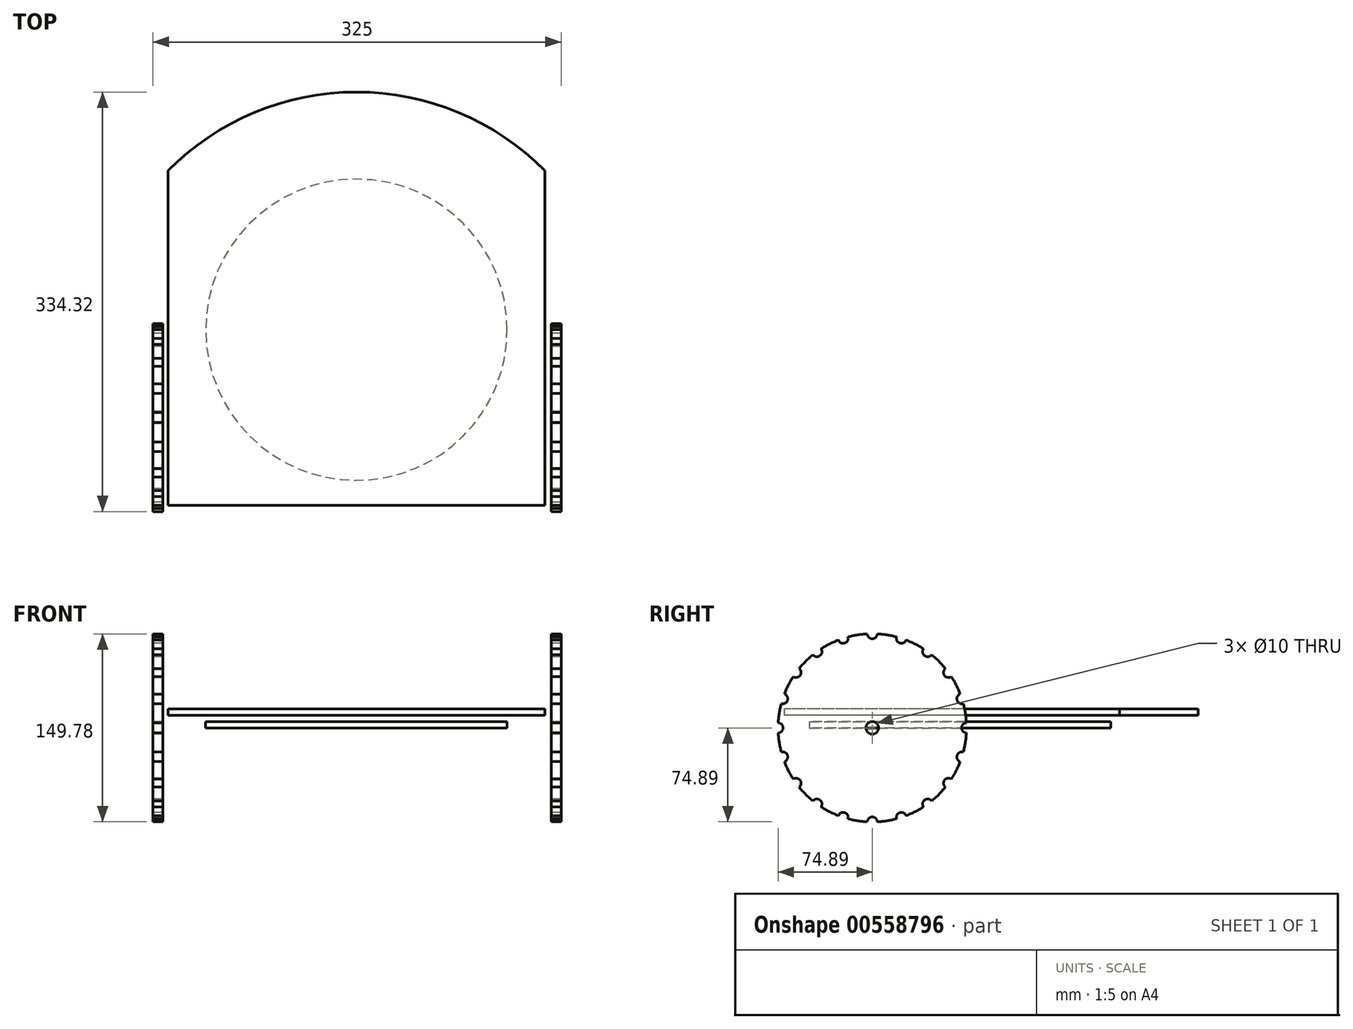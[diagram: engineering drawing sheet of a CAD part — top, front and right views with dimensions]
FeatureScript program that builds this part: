
annotation { "Feature Type Name" : "Feature", "Feature Type Description" : "" }
export const myFeature = defineFeature(function(context is Context, id is Id, definition is map)
    precondition{}
    {
        {
            var Q0;
            Q0=qCreatedBy(makeId("Top.planeOp"),FACE);
            var sketch = newSketch(context, id + "F0", { "sketchPlane" : qUnion([Q0])});
            skCircle(sketch, "E0", {"center": v(0, 0) * mm, "radius": 120 * mm});
            skLineSegment(sketch, "E1.filletArc", {"start": v(150, -145) * mm, "end": v(150, -145) * mm});
            skLineSegment(sketch, "E2", {"start": v(-150, 126.83) * mm, "end": v(150, 126.83) * mm});
            skArc(sketch, "E3", {"start": v(150, 126.83) * mm, "mid": v(0, 189.43) * mm, "end": v(-150, 126.83) * mm});
            skLineSegment(sketch, "E4.top", {"start": v(-150, -140) * mm, "end": v(150, -140) * mm});
            skLineSegment(sketch, "E4.left", {"start": v(-150, 126.83) * mm, "end": v(-150, -140) * mm});
            skLineSegment(sketch, "E4.right", {"start": v(150, 126.83) * mm, "end": v(150, -140) * mm});
            skSolve(sketch);
        }
        {
            var Q0;
            Q0=makeQuery(id+"F0.imprint","IMPRINT",FACE,{"disambiguationData":[TD([[makeQuery(id+"F0.imprint","IMPRINT",EDGE,{"derivedFrom":sQuery(id+"F0.wireOp",EDGE,"E0")}),1.0]])]});
            extrude(context, id + "F1", {"entities" : qUnion([Q0]), "depth" : 5 * mm, "offsetDistance" : 25 * mm});
        }
        {
            var Q0;
            Q0=makeQuery(id+"F0.imprint","IMPRINT",FACE,{"disambiguationData":[TD([[makeQuery(id+"F0.imprint","IMPRINT",EDGE,{"derivedFrom":sQuery(id+"F0.wireOp",EDGE,"E3")}),1.0]])]});
            var Q1;
            Q1=makeQuery(id+"F0.imprint","IMPRINT",FACE,{"disambiguationData":[TD([[makeQuery(id+"F0.imprint","IMPRINT",EDGE,{"derivedFrom":sQuery(id+"F0.wireOp",EDGE,"E0")}),-1.0]])]});
            var Q2;
            Q2=makeQuery(id+"F0.imprint","IMPRINT",FACE,{"disambiguationData":[TD([[makeQuery(id+"F0.imprint","IMPRINT",EDGE,{"derivedFrom":sQuery(id+"F0.wireOp",EDGE,"E0")}),1.0]])]});
            extrude(context, id + "F2", {"entities" : qUnion([Q0, Q1, Q2]), "depth" : 5 * mm, "offsetDistance" : 25 * mm});
        }
        {
            var Q0;
            Q0=makeQuery(id+"F2.opExtrude","SWEPT_BODY",BODY,{"disambiguationData":[OSD([sQuery(id+"F0.wireOp",EDGE,"E3"),sQuery(id+"F0.wireOp",EDGE,"E4.top"),sQuery(id+"F0.wireOp",EDGE,"E4.left"),sQuery(id+"F0.wireOp",EDGE,"E4.right")])]});
            transform(context, id + "F3", {"entities" : qUnion([Q0]), "transformType" : TransformType.TRANSLATION_3D, "dx" : 0 * mm, "dy" : 0 * mm, "dz" : 10 * mm, "makeCopy" : false});
        }
        {
            var Q0;
            Q0=qCreatedBy(makeId("Right.planeOp"),FACE);
            var sketch = newSketch(context, id + "F4", { "sketchPlane" : qUnion([Q0])});
            skCircle(sketch, "E5", {"center": v(0, 0) * mm, "radius": 75 * mm});
            skCircle(sketch, "E6", {"center": v(0, 75) * mm, "radius": 4 * mm});
            skCircle(sketch, "E7.1.0", {"center": v(-23.18, 71.33) * mm, "radius": 4 * mm});
            skCircle(sketch, "E7.2.0", {"center": v(-44.08, 60.68) * mm, "radius": 4 * mm});
            skCircle(sketch, "E7.3.0", {"center": v(-60.68, 44.08) * mm, "radius": 4 * mm});
            skCircle(sketch, "E7.4.0", {"center": v(-71.33, 23.18) * mm, "radius": 4 * mm});
            skCircle(sketch, "E7.5.0", {"center": v(-75, 0) * mm, "radius": 4 * mm});
            skCircle(sketch, "E7.6.0", {"center": v(-71.33, -23.18) * mm, "radius": 4 * mm});
            skCircle(sketch, "E7.7.0", {"center": v(-60.68, -44.08) * mm, "radius": 4 * mm});
            skCircle(sketch, "E7.8.0", {"center": v(-44.08, -60.68) * mm, "radius": 4 * mm});
            skCircle(sketch, "E7.9.0", {"center": v(-23.18, -71.33) * mm, "radius": 4 * mm});
            skCircle(sketch, "E7.10.0", {"center": v(0, -75) * mm, "radius": 4 * mm});
            skCircle(sketch, "E7.11.0", {"center": v(23.18, -71.33) * mm, "radius": 4 * mm});
            skCircle(sketch, "E7.12.0", {"center": v(44.08, -60.68) * mm, "radius": 4 * mm});
            skCircle(sketch, "E7.13.0", {"center": v(60.68, -44.08) * mm, "radius": 4 * mm});
            skCircle(sketch, "E7.14.0", {"center": v(71.33, -23.18) * mm, "radius": 4 * mm});
            skCircle(sketch, "E7.15.0", {"center": v(75, 0) * mm, "radius": 4 * mm});
            skCircle(sketch, "E7.16.0", {"center": v(71.33, 23.18) * mm, "radius": 4 * mm});
            skCircle(sketch, "E7.17.0", {"center": v(60.68, 44.08) * mm, "radius": 4 * mm});
            skCircle(sketch, "E7.18.0", {"center": v(44.08, 60.68) * mm, "radius": 4 * mm});
            skCircle(sketch, "E7.19.0", {"center": v(23.18, 71.33) * mm, "radius": 4 * mm});
            skCircle(sketch, "E8", {"center": v(0, 0) * mm, "radius": 5 * mm});
            skSolve(sketch);
        }
        {
            var Q0;
            {var subQ0=sQuery(id+"F4.wireOp",EDGE,"E5");var subQ40=sQuery(id+"F4.wireOp",EDGE,"E6");var subQ41=makeQuery(id+"F4.imprint","INTERSECT",VERTEX,{"disambiguationData":[OD(0.0)],"derivedFrom":[subQ40,subQ0]});Q0=makeQuery(id+"F4.imprint","IMPRINT",FACE,{"disambiguationData":[TD([[makeQuery(id+"F4.imprint","IMPRINT",EDGE,{"disambiguationData":[TD([[subQ41,1.0]])],"derivedFrom":subQ40}),-1.0]])]});}
            extrude(context, id + "F5", {"entities" : qUnion([Q0]), "depth" : 8 * mm, "offsetDistance" : 25 * mm});
        }
        {
            var Q0;
            Q0=makeQuery(id+"F5.opExtrude","SWEPT_BODY",BODY,{"disambiguationData":[OSD([sQuery(id+"F4.wireOp",EDGE,"E6"),sQuery(id+"F4.wireOp",EDGE,"E7.1.0"),sQuery(id+"F4.wireOp",EDGE,"E7.2.0"),sQuery(id+"F4.wireOp",EDGE,"E7.3.0"),sQuery(id+"F4.wireOp",EDGE,"E7.4.0"),sQuery(id+"F4.wireOp",EDGE,"E7.5.0"),sQuery(id+"F4.wireOp",EDGE,"E7.6.0"),sQuery(id+"F4.wireOp",EDGE,"E7.7.0"),sQuery(id+"F4.wireOp",EDGE,"E7.8.0"),sQuery(id+"F4.wireOp",EDGE,"E7.9.0"),sQuery(id+"F4.wireOp",EDGE,"E7.10.0"),sQuery(id+"F4.wireOp",EDGE,"E7.11.0"),sQuery(id+"F4.wireOp",EDGE,"E7.12.0"),sQuery(id+"F4.wireOp",EDGE,"E7.13.0"),sQuery(id+"F4.wireOp",EDGE,"E7.14.0"),sQuery(id+"F4.wireOp",EDGE,"E7.15.0"),sQuery(id+"F4.wireOp",EDGE,"E7.16.0"),sQuery(id+"F4.wireOp",EDGE,"E7.17.0"),sQuery(id+"F4.wireOp",EDGE,"E7.18.0"),sQuery(id+"F4.wireOp",EDGE,"E7.19.0"),sQuery(id+"F4.wireOp",EDGE,"E5")])]});
            transform(context, id + "F6", {"entities" : qUnion([Q0]), "transformType" : TransformType.TRANSLATION_3D, "dx" : 155 * mm, "dy" : 0 * mm, "dz" : 0 * mm, "makeCopy" : false});
        }
        {
            var Q0;
            Q0=makeQuery(id+"F5.opExtrude","SWEPT_BODY",BODY,{"disambiguationData":[OSD([sQuery(id+"F4.wireOp",EDGE,"E6"),sQuery(id+"F4.wireOp",EDGE,"E7.1.0"),sQuery(id+"F4.wireOp",EDGE,"E7.2.0"),sQuery(id+"F4.wireOp",EDGE,"E7.3.0"),sQuery(id+"F4.wireOp",EDGE,"E7.4.0"),sQuery(id+"F4.wireOp",EDGE,"E7.5.0"),sQuery(id+"F4.wireOp",EDGE,"E7.6.0"),sQuery(id+"F4.wireOp",EDGE,"E7.7.0"),sQuery(id+"F4.wireOp",EDGE,"E7.8.0"),sQuery(id+"F4.wireOp",EDGE,"E7.9.0"),sQuery(id+"F4.wireOp",EDGE,"E7.10.0"),sQuery(id+"F4.wireOp",EDGE,"E7.11.0"),sQuery(id+"F4.wireOp",EDGE,"E7.12.0"),sQuery(id+"F4.wireOp",EDGE,"E7.13.0"),sQuery(id+"F4.wireOp",EDGE,"E7.14.0"),sQuery(id+"F4.wireOp",EDGE,"E7.15.0"),sQuery(id+"F4.wireOp",EDGE,"E7.16.0"),sQuery(id+"F4.wireOp",EDGE,"E7.17.0"),sQuery(id+"F4.wireOp",EDGE,"E7.18.0"),sQuery(id+"F4.wireOp",EDGE,"E7.19.0"),sQuery(id+"F4.wireOp",EDGE,"E5")])]});
            var Q1;
            Q1=makeQuery(id+"F2.opExtrude","CAP_EDGE",EDGE,{"disambiguationData":[OSD([sQuery(id+"F0.wireOp",EDGE,"E4.right")])],"isStart":false});
            var Q2;
            Q2=makeQuery(id+"F2.opExtrude","CAP_EDGE",EDGE,{"disambiguationData":[OSD([sQuery(id+"F0.wireOp",EDGE,"E4.left")])],"isStart":false});
            transform(context, id + "F7", {"entities" : qUnion([Q0]), "transformType" : TransformType.TRANSLATION_3D, "dx" : 0 * mm, "dy" : -70 * mm, "dz" : 0 * mm, "makeCopy" : false});
        }
        {
            var Q0;
            Q0=makeQuery(id+"F5.opExtrude","SWEPT_BODY",BODY,{"disambiguationData":[OSD([sQuery(id+"F4.wireOp",EDGE,"E6"),sQuery(id+"F4.wireOp",EDGE,"E7.1.0"),sQuery(id+"F4.wireOp",EDGE,"E7.2.0"),sQuery(id+"F4.wireOp",EDGE,"E7.3.0"),sQuery(id+"F4.wireOp",EDGE,"E7.4.0"),sQuery(id+"F4.wireOp",EDGE,"E7.5.0"),sQuery(id+"F4.wireOp",EDGE,"E7.6.0"),sQuery(id+"F4.wireOp",EDGE,"E7.7.0"),sQuery(id+"F4.wireOp",EDGE,"E7.8.0"),sQuery(id+"F4.wireOp",EDGE,"E7.9.0"),sQuery(id+"F4.wireOp",EDGE,"E7.10.0"),sQuery(id+"F4.wireOp",EDGE,"E7.11.0"),sQuery(id+"F4.wireOp",EDGE,"E7.12.0"),sQuery(id+"F4.wireOp",EDGE,"E7.13.0"),sQuery(id+"F4.wireOp",EDGE,"E7.14.0"),sQuery(id+"F4.wireOp",EDGE,"E7.15.0"),sQuery(id+"F4.wireOp",EDGE,"E7.16.0"),sQuery(id+"F4.wireOp",EDGE,"E7.17.0"),sQuery(id+"F4.wireOp",EDGE,"E7.18.0"),sQuery(id+"F4.wireOp",EDGE,"E7.19.0"),sQuery(id+"F4.wireOp",EDGE,"E5")])]});
            transform(context, id + "F8", {"entities" : qUnion([Q0]), "transformType" : TransformType.COPY});
        }
        {
            var Q0;
            Q0=makeQuery(id+"F5.opExtrude","SWEPT_BODY",BODY,{"disambiguationData":[OSD([sQuery(id+"F4.wireOp",EDGE,"E6"),sQuery(id+"F4.wireOp",EDGE,"E7.1.0"),sQuery(id+"F4.wireOp",EDGE,"E7.2.0"),sQuery(id+"F4.wireOp",EDGE,"E7.3.0"),sQuery(id+"F4.wireOp",EDGE,"E7.4.0"),sQuery(id+"F4.wireOp",EDGE,"E7.5.0"),sQuery(id+"F4.wireOp",EDGE,"E7.6.0"),sQuery(id+"F4.wireOp",EDGE,"E7.7.0"),sQuery(id+"F4.wireOp",EDGE,"E7.8.0"),sQuery(id+"F4.wireOp",EDGE,"E7.9.0"),sQuery(id+"F4.wireOp",EDGE,"E7.10.0"),sQuery(id+"F4.wireOp",EDGE,"E7.11.0"),sQuery(id+"F4.wireOp",EDGE,"E7.12.0"),sQuery(id+"F4.wireOp",EDGE,"E7.13.0"),sQuery(id+"F4.wireOp",EDGE,"E7.14.0"),sQuery(id+"F4.wireOp",EDGE,"E7.15.0"),sQuery(id+"F4.wireOp",EDGE,"E7.16.0"),sQuery(id+"F4.wireOp",EDGE,"E7.17.0"),sQuery(id+"F4.wireOp",EDGE,"E7.18.0"),sQuery(id+"F4.wireOp",EDGE,"E7.19.0"),sQuery(id+"F4.wireOp",EDGE,"E5")])]});
            transform(context, id + "F9", {"entities" : qUnion([Q0]), "transformType" : TransformType.TRANSLATION_3D, "dx" : -317 * mm, "dy" : 0 * mm, "dz" : 0 * mm, "makeCopy" : true});
        }
        {
            var Q0;
            Q0=makeQuery(id+"F5.opExtrude","CAP_FACE",FACE,{"disambiguationData":[OSD([sQuery(id+"F4.wireOp",EDGE,"E6"),sQuery(id+"F4.wireOp",EDGE,"E7.1.0"),sQuery(id+"F4.wireOp",EDGE,"E7.2.0"),sQuery(id+"F4.wireOp",EDGE,"E7.3.0"),sQuery(id+"F4.wireOp",EDGE,"E7.4.0"),sQuery(id+"F4.wireOp",EDGE,"E7.5.0"),sQuery(id+"F4.wireOp",EDGE,"E7.6.0"),sQuery(id+"F4.wireOp",EDGE,"E7.7.0"),sQuery(id+"F4.wireOp",EDGE,"E7.8.0"),sQuery(id+"F4.wireOp",EDGE,"E7.9.0"),sQuery(id+"F4.wireOp",EDGE,"E7.10.0"),sQuery(id+"F4.wireOp",EDGE,"E7.11.0"),sQuery(id+"F4.wireOp",EDGE,"E7.12.0"),sQuery(id+"F4.wireOp",EDGE,"E7.13.0"),sQuery(id+"F4.wireOp",EDGE,"E7.14.0"),sQuery(id+"F4.wireOp",EDGE,"E7.15.0"),sQuery(id+"F4.wireOp",EDGE,"E7.16.0"),sQuery(id+"F4.wireOp",EDGE,"E7.17.0"),sQuery(id+"F4.wireOp",EDGE,"E7.18.0"),sQuery(id+"F4.wireOp",EDGE,"E7.19.0"),sQuery(id+"F4.wireOp",EDGE,"E5")])],"isStart":false});
            var sketch = newSketch(context, id + "F10", { "sketchPlane" : qUnion([Q0])});
            skCircle(sketch, "E9", {"center": v(-70, 0) * mm, "radius": 5 * mm});
            skSolve(sketch);
        }
        {
            var Q0;
            Q0=makeQuery(id+"F10.imprint","IMPRINT",FACE,{"disambiguationData":[TD([[makeQuery(id+"F10.imprint","IMPRINT",EDGE,{"derivedFrom":sQuery(id+"F10.wireOp",EDGE,"E9")}),1.0]])]});
            extrude(context, id + "F11", {"entities" : qUnion([Q0]), "operationType" : NewBodyOperationType.REMOVE, "oppositeDirection" : true, "depth" : 25 * mm, "offsetDistance" : 25 * mm});
        }
    });
